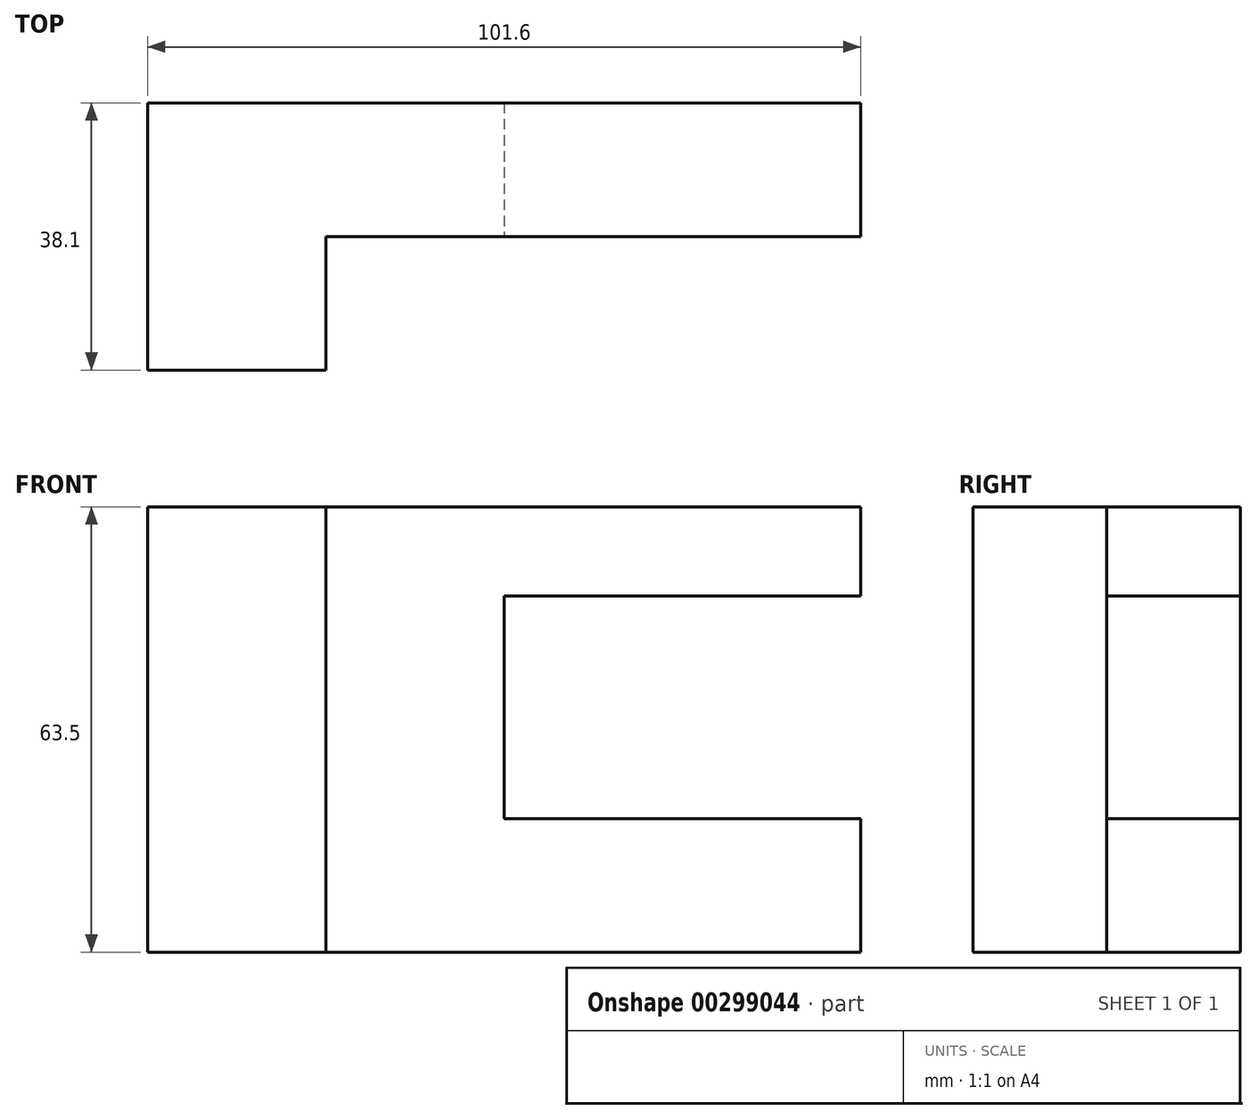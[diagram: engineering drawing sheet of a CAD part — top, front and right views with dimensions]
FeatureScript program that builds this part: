
annotation { "Feature Type Name" : "Feature", "Feature Type Description" : "" }
export const myFeature = defineFeature(function(context is Context, id is Id, definition is map)
    precondition{}
    {
        {
            var Q0;
            Q0=qCreatedBy(makeId("Front.planeOp"),FACE);
            var sketch = newSketch(context, id + "F0", { "sketchPlane" : qUnion([Q0])});
            skLineSegment(sketch, "E0.bottom", {"start": v(50.8, -31.75) * mm, "end": v(-50.8, -31.75) * mm});
            skLineSegment(sketch, "E0.top", {"start": v(50.8, 31.75) * mm, "end": v(-50.8, 31.75) * mm});
            skLineSegment(sketch, "E0.left", {"start": v(50.8, -31.75) * mm, "end": v(50.8, 31.75) * mm});
            skLineSegment(sketch, "E0.right", {"start": v(-50.8, -31.75) * mm, "end": v(-50.8, 31.75) * mm});
            skPoint(sketch, "E0.middle", {"position": v(0, 0) * mm});
            skSolve(sketch);
        }
        {
            var Q0;
            Q0 = qSketchRegion(id + "F0", true);
            extrude(context, id + "F1", {"entities" : qUnion([Q0]), "depth" : 19.05 * mm});
        }
        {
            var Q0;
            Q0=makeQuery(id+"F1.opExtrude","CAP_FACE",FACE,{"disambiguationData":[OSD([sQuery(id+"F0.wireOp",EDGE,"E0.bottom"),sQuery(id+"F0.wireOp",EDGE,"E0.top"),sQuery(id+"F0.wireOp",EDGE,"E0.left"),sQuery(id+"F0.wireOp",EDGE,"E0.right")])],"isStart":false});
            var sketch = newSketch(context, id + "F2", { "sketchPlane" : qUnion([Q0])});
            skLineSegment(sketch, "E1.bottom", {"start": v(-25.4, 31.75) * mm, "end": v(-50.8, 31.75) * mm});
            skLineSegment(sketch, "E1.top", {"start": v(-25.4, -31.75) * mm, "end": v(-50.8, -31.75) * mm});
            skLineSegment(sketch, "E1.left", {"start": v(-25.4, 31.75) * mm, "end": v(-25.4, -31.75) * mm});
            skLineSegment(sketch, "E1.right", {"start": v(-50.8, 31.75) * mm, "end": v(-50.8, -31.75) * mm});
            skSolve(sketch);
        }
        {
            var Q0;
            Q0=makeQuery(id+"F2.imprint","IMPRINT",FACE,{"disambiguationData":[TD([[makeQuery(id+"F2.imprint","IMPRINT",EDGE,{"derivedFrom":sQuery(id+"F2.wireOp",EDGE,"E1.bottom")}),1.0]])]});
            extrude(context, id + "F3", {"entities" : qUnion([Q0]), "operationType" : NewBodyOperationType.ADD, "depth" : 19.05 * mm});
        }
        {
            var Q0;
            Q0=makeQuery(id+"F1.opExtrude","CAP_FACE",FACE,{"disambiguationData":[OSD([sQuery(id+"F0.wireOp",EDGE,"E0.bottom"),sQuery(id+"F0.wireOp",EDGE,"E0.top"),sQuery(id+"F0.wireOp",EDGE,"E0.left"),sQuery(id+"F0.wireOp",EDGE,"E0.right")])],"isStart":false});
            var sketch = newSketch(context, id + "F4", { "sketchPlane" : qUnion([Q0])});
            skLineSegment(sketch, "E2.bottom", {"start": v(50.8, 19.05) * mm, "end": v(0, 19.05) * mm});
            skLineSegment(sketch, "E2.top", {"start": v(50.8, -12.7) * mm, "end": v(0, -12.7) * mm});
            skLineSegment(sketch, "E2.left", {"start": v(50.8, 19.05) * mm, "end": v(50.8, -12.7) * mm});
            skLineSegment(sketch, "E2.right", {"start": v(0, 19.05) * mm, "end": v(0, -12.7) * mm});
            skSolve(sketch);
        }
        {
            var Q0;
            Q0=makeQuery(id+"F4.imprint","IMPRINT",FACE,{"disambiguationData":[TD([[makeQuery(id+"F4.imprint","IMPRINT",EDGE,{"derivedFrom":sQuery(id+"F4.wireOp",EDGE,"E2.bottom")}),1.0]])]});
            extrude(context, id + "F5", {"entities" : qUnion([Q0]), "operationType" : NewBodyOperationType.REMOVE, "endBound" : BoundingType.THROUGH_ALL, "oppositeDirection" : true, "depth" : 25.4 * mm});
        }
    });
